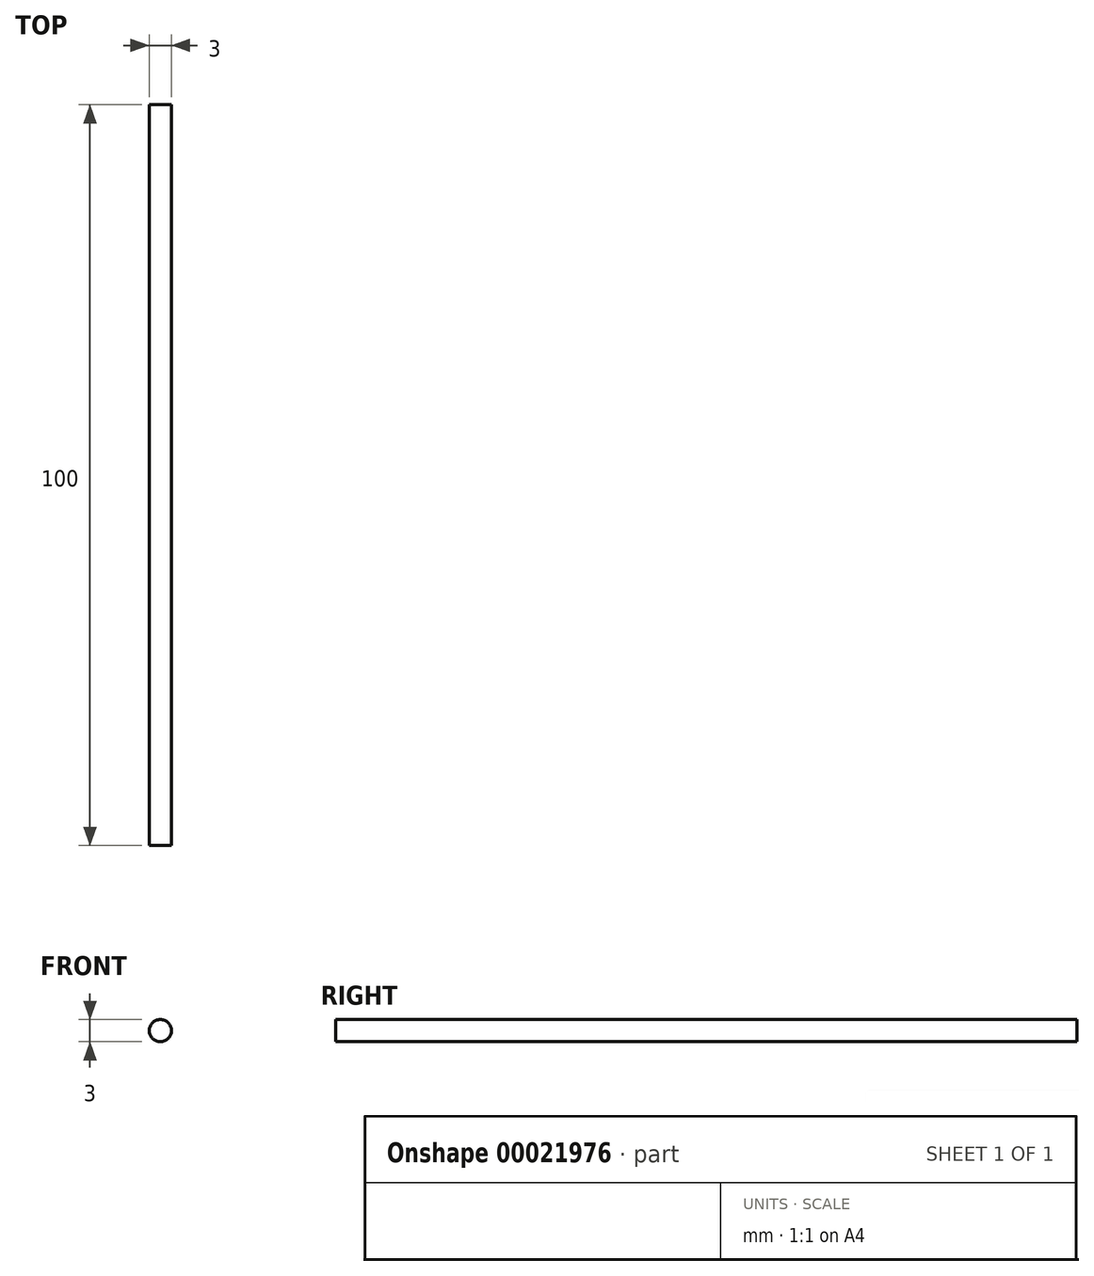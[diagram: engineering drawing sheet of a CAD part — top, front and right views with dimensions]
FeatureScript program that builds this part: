
annotation { "Feature Type Name" : "Feature", "Feature Type Description" : "" }
export const myFeature = defineFeature(function(context is Context, id is Id, definition is map)
    precondition{}
    {
        {
            var Q0;
            Q0=qCreatedBy(makeId("Front.planeOp"),FACE);
            var sketch = newSketch(context, id + "F0", { "sketchPlane" : qUnion([Q0])});
            skCircle(sketch, "E0", {"center": v(-17.12, -2.64) * mm, "radius": 1.5 * mm});
            skSolve(sketch);
        }
        {
            var Q0;
            Q0 = qSketchRegion(id + "F0", true);
            extrude(context, id + "F1", {"entities" : qUnion([Q0]), "depth" : 100 * mm});
        }
    });
